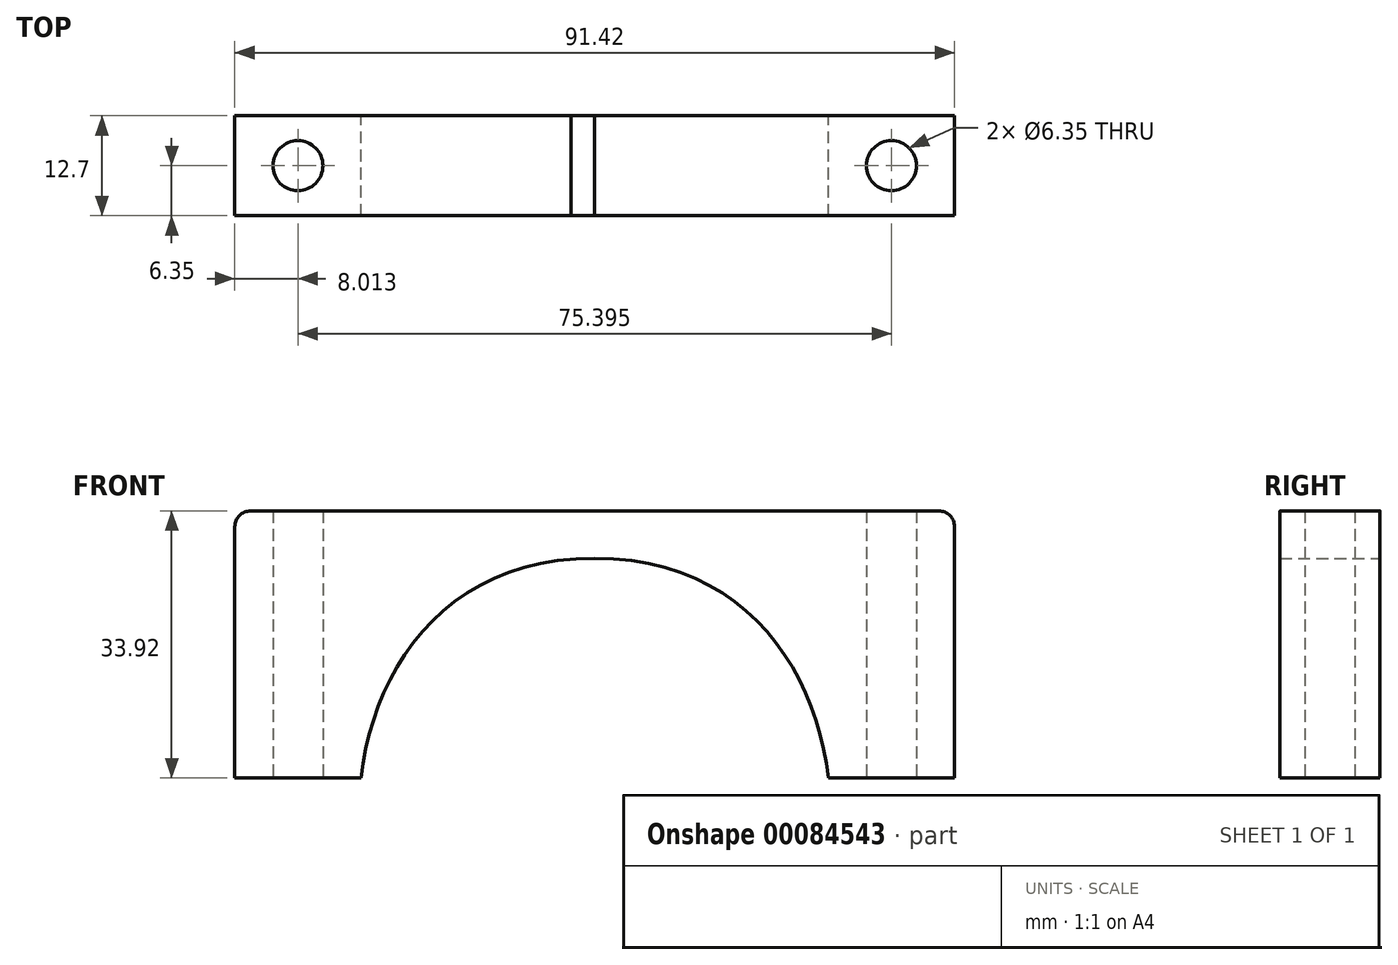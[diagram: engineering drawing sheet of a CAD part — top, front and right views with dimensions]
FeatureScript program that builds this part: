
annotation { "Feature Type Name" : "Feature", "Feature Type Description" : "" }
export const myFeature = defineFeature(function(context is Context, id is Id, definition is map)
    precondition{}
    {
        {
            var Q0;
            Q0=qCreatedBy(makeId("Front.planeOp"),FACE);
            var sketch = newSketch(context, id + "F0", { "sketchPlane" : qUnion([Q0]) });
            skPoint(sketch, "E0", {"position": v(0.75, 6.5) * mm});
            skPoint(sketch, "E1", {"position": v(2.8, 12.5) * mm});
            skPoint(sketch, "E2", {"position": v(7, 21.8) * mm});
            skPoint(sketch, "E3", {"position": v(12.7, 27.2) * mm});
            skPoint(sketch, "E4", {"position": v(17.2, 29.2) * mm});
            skPoint(sketch, "E5", {"position": v(22.2, 30.8) * mm});
            skPoint(sketch, "E6", {"position": v(30, 32.9) * mm});
            skFitSpline(sketch, "E7", {"points": [v(0, 0) * mm, v(30, 32.9) * mm], "startDerivative": vector(0, 47.28) * mm, "endDerivative": vector(63, 0) * mm});
            skLineSegment(sketch, "E8", {"start": v(30, 32.9) * mm, "end": v(-9.5, 32.9) * mm, "construction": true});
            skLineSegment(sketch, "E9", {"start": v(30, 32.9) * mm, "end": v(30, 0) * mm, "construction": true});
            skFitSpline(sketch, "E10.MirrorCS", {"points": [v(60, 0) * mm, v(30, 32.9) * mm], "startDerivative": vector(0, 47.28) * mm, "endDerivative": vector(-63, 0) * mm});
            skFitSpline(sketch, "E11.0", {"points": [v(66, 0) * mm, v(66, 2.26) * mm, v(65.68, 6.8) * mm, v(64.18, 13.59) * mm, v(61.6, 20.12) * mm, v(57.82, 26.18) * mm, v(52.76, 31.46) * mm, v(46.38, 35.62) * mm, v(38.79, 38.28) * mm, v(33.03, 38.9) * mm, v(30, 38.9) * mm]});
            skFitSpline(sketch, "E11.1", {"points": [v(-6, 0) * mm, v(-6, 2.26) * mm, v(-5.68, 6.8) * mm, v(-4.18, 13.59) * mm, v(-1.6, 20.12) * mm, v(2.18, 26.18) * mm, v(7.24, 31.46) * mm, v(13.62, 35.62) * mm, v(21.21, 38.28) * mm, v(26.97, 38.9) * mm, v(30, 38.9) * mm]});
            skLineSegment(sketch, "E12", {"start": v(0, 0) * mm, "end": v(-6, 0) * mm});
            skLineSegment(sketch, "E13.MirrorCS", {"start": v(60, 0) * mm, "end": v(66, 0) * mm});
            skLineSegment(sketch, "E14.trimOffspring", {"start": v(0.3, 5) * mm, "end": v(59.7, 5) * mm});
            skLineSegment(sketch, "E15", {"start": v(0.3, 5) * mm, "end": v(-15.7, 5) * mm});
            skLineSegment(sketch, "E16", {"start": v(-15.7, 5) * mm, "end": v(-15.7, 38.9) * mm});
            skLineSegment(sketch, "E17", {"start": v(-15.7, 38.9) * mm, "end": v(30, 38.9) * mm});
            skLineSegment(sketch, "E18.MirrorCS", {"start": v(75.7, 38.9) * mm, "end": v(30, 38.9) * mm});
            skLineSegment(sketch, "E19.MirrorCS", {"start": v(75.7, 5) * mm, "end": v(75.7, 38.9) * mm});
            skLineSegment(sketch, "E20.MirrorCS", {"start": v(59.7, 5) * mm, "end": v(75.7, 5) * mm});
            skLineSegment(sketch, "E21", {"start": v(-15.7, 38.9) * mm, "end": v(-15.7, 39.9) * mm});
            skLineSegment(sketch, "E22", {"start": v(-15.7, 39.9) * mm, "end": v(75.7, 39.9) * mm});
            skLineSegment(sketch, "E23", {"start": v(75.7, 39.9) * mm, "end": v(75.7, 38.9) * mm});
            skSolve(sketch);
        }
        {
            var Q0;
            {var subQ6=sQuery(id+"F0.wireOp",EDGE,"E10.MirrorCS");var subQ7=sQuery(id+"F0.wireOp",EDGE,"E7");var subQ8=makeQuery(id+"F0.imprint","INTERSECT",VERTEX,{"derivedFrom":[subQ7,subQ6]});Q0=makeQuery(id+"F0.imprint","IMPRINT",FACE,{"disambiguationData":[TD([[makeQuery(id+"F0.imprint","IMPRINT",EDGE,{"disambiguationData":[TD([[subQ8,1.0]])],"derivedFrom":subQ7}),1.0]])]});}
            var Q1;
            {var subQ4=sQuery(id+"F0.wireOp",EDGE,"E16");Q1=makeQuery(id+"F0.imprint","IMPRINT",FACE,{"disambiguationData":[TD([[makeQuery(id+"F0.imprint","IMPRINT",EDGE,{"derivedFrom":subQ4}),-1.0]])]});}
            var Q2;
            {var subQ0=sQuery(id+"F0.wireOp",EDGE,"E18.MirrorCS");Q2=makeQuery(id+"F0.imprint","IMPRINT",FACE,{"disambiguationData":[TD([[makeQuery(id+"F0.imprint","IMPRINT",EDGE,{"derivedFrom":subQ0}),1.0]])]});}
            var Q3;
            Q3=makeQuery(id+"F0.imprint","IMPRINT",FACE,{"disambiguationData":[TD([[makeQuery(id+"F0.imprint","IMPRINT",EDGE,{"derivedFrom":sQuery(id+"F0.wireOp",EDGE,"E17")}),1.0]])]});
            extrude(context, id + "F1", {"entities" : qUnion([Q0, Q1, Q2, Q3]), "depth" : 12.7 * mm});
        }
        {
            var Q0;
            Q0=makeQuery(id+"F1.opExtrude","SWEPT_FACE",FACE,{"disambiguationData":[OSD([sQuery(id+"F0.wireOp",EDGE,"E15")])]});
            var sketch = newSketch(context, id + "F2", { "sketchPlane" : qUnion([Q0]) });
            skCircle(sketch, "E24", {"center": v(-7.7, 6.35) * mm, "radius": 3.18 * mm});
            skPoint(sketch, "E24.centerSnap0", {"position": v(0.3, 6.35) * mm});
            skSolve(sketch);
        }
        {
            var Q0;
            Q0 = qSketchRegion(id + "F2", true);
            extrude(context, id + "F3", {"entities" : qUnion([Q0]), "operationType" : NewBodyOperationType.REMOVE, "endBound" : BoundingType.UP_TO_NEXT, "oppositeDirection" : true, "depth" : 25 * mm});
        }
        {
            var Q0;
            Q0=makeQuery(id+"F1.opExtrude","SWEPT_FACE",FACE,{"disambiguationData":[OSD([sQuery(id+"F0.wireOp",EDGE,"E20.MirrorCS")])]});
            var sketch = newSketch(context, id + "F4", { "sketchPlane" : qUnion([Q0]) });
            skCircle(sketch, "E25", {"center": v(67.7, 6.35) * mm, "radius": 3.18 * mm});
            skPoint(sketch, "E25.centerSnap0", {"position": v(75.7, 6.35) * mm});
            skSolve(sketch);
        }
        {
            var Q0;
            Q0 = qSketchRegion(id + "F4", true);
            extrude(context, id + "F5", {"entities" : qUnion([Q0]), "operationType" : NewBodyOperationType.REMOVE, "endBound" : BoundingType.UP_TO_NEXT, "oppositeDirection" : true, "depth" : 25 * mm});
        }
        {
            var Q0;
            Q0=makeQuery(id+"F1.opExtrude","SWEPT_EDGE",EDGE,{"disambiguationData":[OSD([sQuery(id+"F0.wireOp",EDGE,"E21"),sQuery(id+"F0.wireOp",EDGE,"E22")])]});
            var Q1;
            Q1=makeQuery(id+"F1.opExtrude","SWEPT_EDGE",EDGE,{"disambiguationData":[OSD([sQuery(id+"F0.wireOp",EDGE,"E22"),sQuery(id+"F0.wireOp",EDGE,"E23")])]});
            fillet(context, id + "F6", {"entities" : qUnion([Q0, Q1]), "radius" : 2 * mm, "tangentPropagation" : true, "conicFillet" : false});
        }
    });
